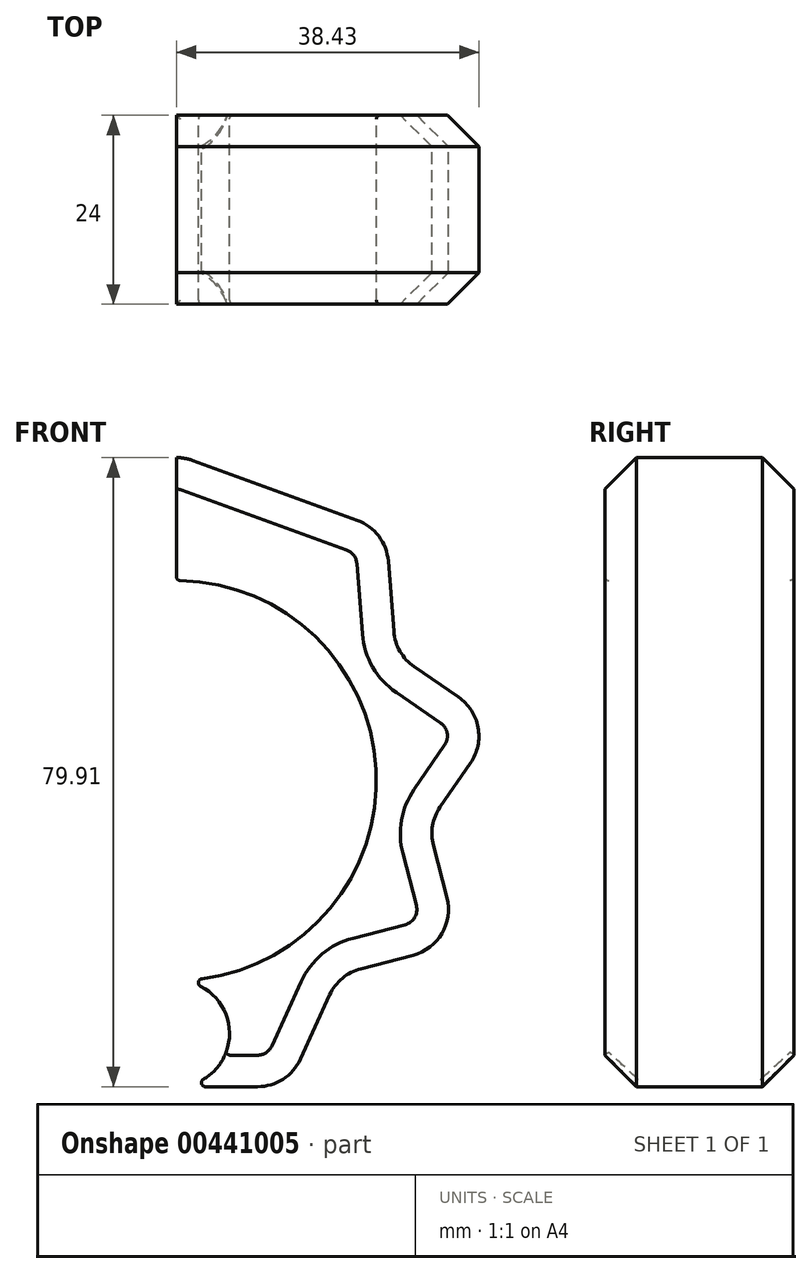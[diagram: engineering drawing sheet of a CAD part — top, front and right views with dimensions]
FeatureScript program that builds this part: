
annotation { "Feature Type Name" : "Feature", "Feature Type Description" : "" }
export const myFeature = defineFeature(function(context is Context, id is Id, definition is map)
    precondition{}
    {
        {
            var Q0;
            Q0=qCreatedBy(makeId("Front.planeOp"),FACE);
            var sketch = newSketch(context, id + "F0", { "sketchPlane" : qUnion([Q0])});
            skCircle(sketch, "E0", {"center": v(0, 0) * mm, "radius": 25.4 * mm});
            skLineSegment(sketch, "E1.0", {"start": v(2.05, 40.65) * mm, "end": v(22.99, 33.03) * mm});
            skLineSegment(sketch, "E1.4", {"start": v(10.3, -38.9) * mm, "end": v(-10.3, -38.9) * mm});
            skLineSegment(sketch, "E1.8", {"start": v(-22.99, 33.03) * mm, "end": v(-2.05, 40.65) * mm});
            skLineSegment(sketch, "E2", {"start": v(33.7, 19.45) * mm, "end": v(22, 12.7) * mm, "construction": true});
            skLineSegment(sketch, "E3", {"start": v(-26.61, 31.71) * mm, "end": v(-16.33, 19.46) * mm, "construction": true});
            skLineSegment(sketch, "E4", {"start": v(26.61, 31.71) * mm, "end": v(16.33, 19.46) * mm, "construction": true});
            skLineSegment(sketch, "E5", {"start": v(-40.77, 7.19) * mm, "end": v(-25.01, 4.41) * mm, "construction": true});
            skLineSegment(sketch, "E6", {"start": v(35.85, -20.7) * mm, "end": v(22, -12.7) * mm, "construction": true});
            skLineSegment(sketch, "E7", {"start": v(40.77, 7.19) * mm, "end": v(25.01, 4.41) * mm, "construction": true});
            skLineSegment(sketch, "E8", {"start": v(-14.16, -38.9) * mm, "end": v(-8.69, -23.87) * mm, "construction": true});
            skLineSegment(sketch, "E9", {"start": v(14.16, -38.9) * mm, "end": v(8.69, -23.87) * mm, "construction": true});
            skLineSegment(sketch, "E10.trimOffspring", {"start": v(8.69, 23.87) * mm, "end": v(13.3, 36.56) * mm, "construction": true});
            skLineSegment(sketch, "E11.trimOffspring", {"start": v(-16.33, -19.46) * mm, "end": v(-25, -29.8) * mm, "construction": true});
            skLineSegment(sketch, "E12.trimOffspring", {"start": v(-25.01, -4.41) * mm, "end": v(-38.31, -6.76) * mm, "construction": true});
            skLineSegment(sketch, "E13.trimOffspring", {"start": v(25.01, -4.41) * mm, "end": v(38.31, -6.76) * mm, "construction": true});
            skLineSegment(sketch, "E14.trimOffspring", {"start": v(-22, 12.7) * mm, "end": v(-33.7, 19.45) * mm, "construction": true});
            skLineSegment(sketch, "E15.trimOffspring", {"start": v(16.33, -19.46) * mm, "end": v(25, -29.8) * mm, "construction": true});
            skLineSegment(sketch, "E16.trimOffspring", {"start": v(-8.69, 23.87) * mm, "end": v(-13.3, 36.56) * mm, "construction": true});
            skLineSegment(sketch, "E17.trimOffspring", {"start": v(-22, -12.7) * mm, "end": v(-35.85, -20.7) * mm, "construction": true});
            skLineSegment(sketch, "E18", {"start": v(15.76, -35.4) * mm, "end": v(19.48, -27.23) * mm});
            skLineSegment(sketch, "E19", {"start": v(23.44, -23.91) * mm, "end": v(30.04, -22.2) * mm});
            skLineSegment(sketch, "E20", {"start": v(34.35, -14.9) * mm, "end": v(32.64, -8.28) * mm});
            skLineSegment(sketch, "E21", {"start": v(33.5, -3.38) * mm, "end": v(37.37, 2.24) * mm});
            skLineSegment(sketch, "E22", {"start": v(35.83, 10.59) * mm, "end": v(30.2, 14.46) * mm});
            skLineSegment(sketch, "E23", {"start": v(27.62, 18.93) * mm, "end": v(26.91, 27.87) * mm});
            skLineSegment(sketch, "E24", {"start": v(-15.76, -35.4) * mm, "end": v(-19.48, -27.23) * mm});
            skLineSegment(sketch, "E25", {"start": v(-23.44, -23.91) * mm, "end": v(-29.94, -22.23) * mm});
            skLineSegment(sketch, "E26", {"start": v(-34.22, -14.82) * mm, "end": v(-32.43, -8.34) * mm});
            skLineSegment(sketch, "E27", {"start": v(-33.32, -3.25) * mm, "end": v(-37.23, 2.22) * mm});
            skLineSegment(sketch, "E28", {"start": v(-35.74, 10.65) * mm, "end": v(-30.2, 14.46) * mm});
            skLineSegment(sketch, "E29", {"start": v(-27.62, 18.93) * mm, "end": v(-26.91, 27.87) * mm});
            skPoint(sketch, "E30.visualSharp", {"position": v(40.77, 7.19) * mm});
            skArc(sketch, "E30.filletArc", {"start": v(37.37, 2.24) * mm, "mid": v(38.33, 6.74) * mm, "end": v(35.83, 10.59) * mm});
            skPoint(sketch, "E31.visualSharp", {"position": v(27.84, 16.08) * mm});
            skArc(sketch, "E31.filletArc", {"start": v(27.62, 18.93) * mm, "mid": v(28.4, 16.4) * mm, "end": v(30.2, 14.46) * mm});
            skPoint(sketch, "E32.visualSharp", {"position": v(26.61, 31.71) * mm});
            skArc(sketch, "E32.filletArc", {"start": v(26.91, 27.87) * mm, "mid": v(25.7, 31.03) * mm, "end": v(22.99, 33.03) * mm});
            skPoint(sketch, "E33.visualSharp", {"position": v(-26.61, 31.71) * mm});
            skArc(sketch, "E33.filletArc", {"start": v(-22.99, 33.03) * mm, "mid": v(-25.7, 31.03) * mm, "end": v(-26.91, 27.87) * mm});
            skPoint(sketch, "E34.visualSharp", {"position": v(-27.84, 16.08) * mm});
            skArc(sketch, "E34.filletArc", {"start": v(-30.2, 14.46) * mm, "mid": v(-28.4, 16.4) * mm, "end": v(-27.62, 18.93) * mm});
            skPoint(sketch, "E35.visualSharp", {"position": v(-40.77, 7.19) * mm});
            skArc(sketch, "E35.filletArc", {"start": v(-35.74, 10.65) * mm, "mid": v(-38.25, 6.74) * mm, "end": v(-37.23, 2.22) * mm});
            skPoint(sketch, "E36.visualSharp", {"position": v(-31.66, -5.58) * mm});
            skArc(sketch, "E36.filletArc", {"start": v(-32.43, -8.34) * mm, "mid": v(-32.3, -5.7) * mm, "end": v(-33.32, -3.25) * mm});
            skPoint(sketch, "E37.visualSharp", {"position": v(-35.85, -20.7) * mm});
            skArc(sketch, "E37.filletArc", {"start": v(-34.22, -14.82) * mm, "mid": v(-33.64, -19.42) * mm, "end": v(-29.94, -22.23) * mm});
            skPoint(sketch, "E38.visualSharp", {"position": v(-14.16, -38.9) * mm});
            skArc(sketch, "E38.filletArc", {"start": v(-15.76, -35.4) * mm, "mid": v(-13.55, -37.95) * mm, "end": v(-10.3, -38.9) * mm});
            skPoint(sketch, "E39.visualSharp", {"position": v(14.16, -38.9) * mm});
            skArc(sketch, "E39.filletArc", {"start": v(10.3, -38.9) * mm, "mid": v(13.55, -37.95) * mm, "end": v(15.76, -35.4) * mm});
            skPoint(sketch, "E40.visualSharp", {"position": v(20.67, -24.63) * mm});
            skArc(sketch, "E40.filletArc", {"start": v(23.44, -23.91) * mm, "mid": v(21.08, -25.13) * mm, "end": v(19.48, -27.23) * mm});
            skPoint(sketch, "E41.visualSharp", {"position": v(31.96, -5.63) * mm});
            skArc(sketch, "E41.filletArc", {"start": v(33.5, -3.38) * mm, "mid": v(32.54, -5.74) * mm, "end": v(32.64, -8.28) * mm});
            skPoint(sketch, "E42.visualSharp", {"position": v(35.85, -20.7) * mm});
            skArc(sketch, "E42.filletArc", {"start": v(30.04, -22.2) * mm, "mid": v(33.71, -19.44) * mm, "end": v(34.35, -14.9) * mm});
            skPoint(sketch, "E43.visualSharp", {"position": v(-20.67, -24.63) * mm});
            skArc(sketch, "E43.filletArc", {"start": v(-19.48, -27.23) * mm, "mid": v(-21.08, -25.13) * mm, "end": v(-23.44, -23.91) * mm});
            skPoint(sketch, "E44.visualSharp", {"position": v(0, 41.4) * mm});
            skArc(sketch, "E44.filletArc", {"start": v(2.05, 40.65) * mm, "mid": v(0, 41.01) * mm, "end": v(-2.05, 40.65) * mm});
            skLineSegment(sketch, "E45", {"start": v(0, 41.01) * mm, "end": v(0, 25.4) * mm});
            skLineSegment(sketch, "E46", {"start": v(0, -38.9) * mm, "end": v(0, -25.4) * mm, "construction": true});
            skCircle(sketch, "E47", {"center": v(0, -32.15) * mm, "radius": 6.75 * mm});
            skSolve(sketch);
        }
        {
            var Q0;
            {var subQ2=sQuery(id+"F0.wireOp",EDGE,"E1.0");Q0=makeQuery(id+"F0.imprint","IMPRINT",FACE,{"disambiguationData":[TD([[makeQuery(id+"F0.imprint","IMPRINT",EDGE,{"derivedFrom":subQ2}),-1.0]])]});}
            extrude(context, id + "F1", {"entities" : qUnion([Q0]), "endBound" : BoundingType.SYMMETRIC, "depth" : 24 * mm});
        }
        {
            var Q0;
            Q0=makeQuery(id+"F1.opExtrude","CAP_EDGE",EDGE,{"disambiguationData":[OSD([sQuery(id+"F0.wireOp",EDGE,"E1.0")])],"isStart":false});
            var Q1;
            Q1=makeQuery(id+"F1.opExtrude","CAP_EDGE",EDGE,{"disambiguationData":[OSD([sQuery(id+"F0.wireOp",EDGE,"E23")])],"isStart":true});
            chamfer(context, id + "F2", {"entities" : qUnion([Q0, Q1]), "width" : 4 * mm, "tangentPropagation" : true});
        }
        {
            var Q0;
            Q0=makeQuery(id+"F1.opExtrude","SWEPT_EDGE",EDGE,{"disambiguationData":[OSD([sQuery(id+"F0.wireOp",EDGE,"E0"),sQuery(id+"F0.wireOp",EDGE,"E47")])]});
            var Q1;
            Q1=makeQuery(id+"F1.opExtrude","SWEPT_EDGE",EDGE,{"disambiguationData":[OSD([sQuery(id+"F0.wireOp",EDGE,"E1.4"),sQuery(id+"F0.wireOp",EDGE,"E47")])]});
            var Q2;
            Q2=makeQuery(id+"F1.opExtrude","CAP_EDGE",EDGE,{"disambiguationData":[OSD([sQuery(id+"F0.wireOp",EDGE,"E47")])],"isStart":false});
            var Q3;
            Q3=makeQuery(id+"F2.opChamfer","BLEND_EDGE",EDGE,{"blendedFrom":[makeQuery(id+"F1.opExtrude","CAP_EDGE",EDGE,{"disambiguationData":[OSD([sQuery(id+"F0.wireOp",EDGE,"E1.4")])],"isStart":false}),makeQuery(id+"F1.opExtrude","SWEPT_FACE",FACE,{"disambiguationData":[OSD([sQuery(id+"F0.wireOp",EDGE,"E47")])]})],"blendedInto":[makeQuery(id+"F1.opExtrude","SWEPT_FACE",FACE,{"disambiguationData":[OSD([sQuery(id+"F0.wireOp",EDGE,"E47")])]})]});
            var Q4;
            Q4=makeQuery(id+"F1.opExtrude","CAP_EDGE",EDGE,{"disambiguationData":[OSD([sQuery(id+"F0.wireOp",EDGE,"E47")])],"isStart":true});
            var Q5;
            Q5=makeQuery(id+"F2.opChamfer","BLEND_EDGE",EDGE,{"blendedFrom":[makeQuery(id+"F1.opExtrude","CAP_EDGE",EDGE,{"disambiguationData":[OSD([sQuery(id+"F0.wireOp",EDGE,"E1.4")])],"isStart":true}),makeQuery(id+"F1.opExtrude","SWEPT_FACE",FACE,{"disambiguationData":[OSD([sQuery(id+"F0.wireOp",EDGE,"E47")])]})],"blendedInto":[makeQuery(id+"F1.opExtrude","SWEPT_FACE",FACE,{"disambiguationData":[OSD([sQuery(id+"F0.wireOp",EDGE,"E47")])]})]});
            var Q6;
            Q6=makeQuery(id+"F1.opExtrude","CAP_EDGE",EDGE,{"disambiguationData":[OSD([sQuery(id+"F0.wireOp",EDGE,"E0")])],"isStart":false});
            var Q7;
            Q7=makeQuery(id+"F1.opExtrude","CAP_EDGE",EDGE,{"disambiguationData":[OSD([sQuery(id+"F0.wireOp",EDGE,"E0")])],"isStart":true});
            var Q8;
            Q8=makeQuery(id+"F1.opExtrude","SWEPT_EDGE",EDGE,{"disambiguationData":[OSD([sQuery(id+"F0.wireOp",EDGE,"E0"),sQuery(id+"F0.wireOp",EDGE,"E45")])]});
            fillet(context, id + "F3", {"entities" : qUnion([Q0, Q1, Q2, Q3, Q4, Q5, Q6, Q7, Q8]), "radius" : .5 * mm, "tangentPropagation" : true, "allowEdgeOverflow" : false});
        }
    });
